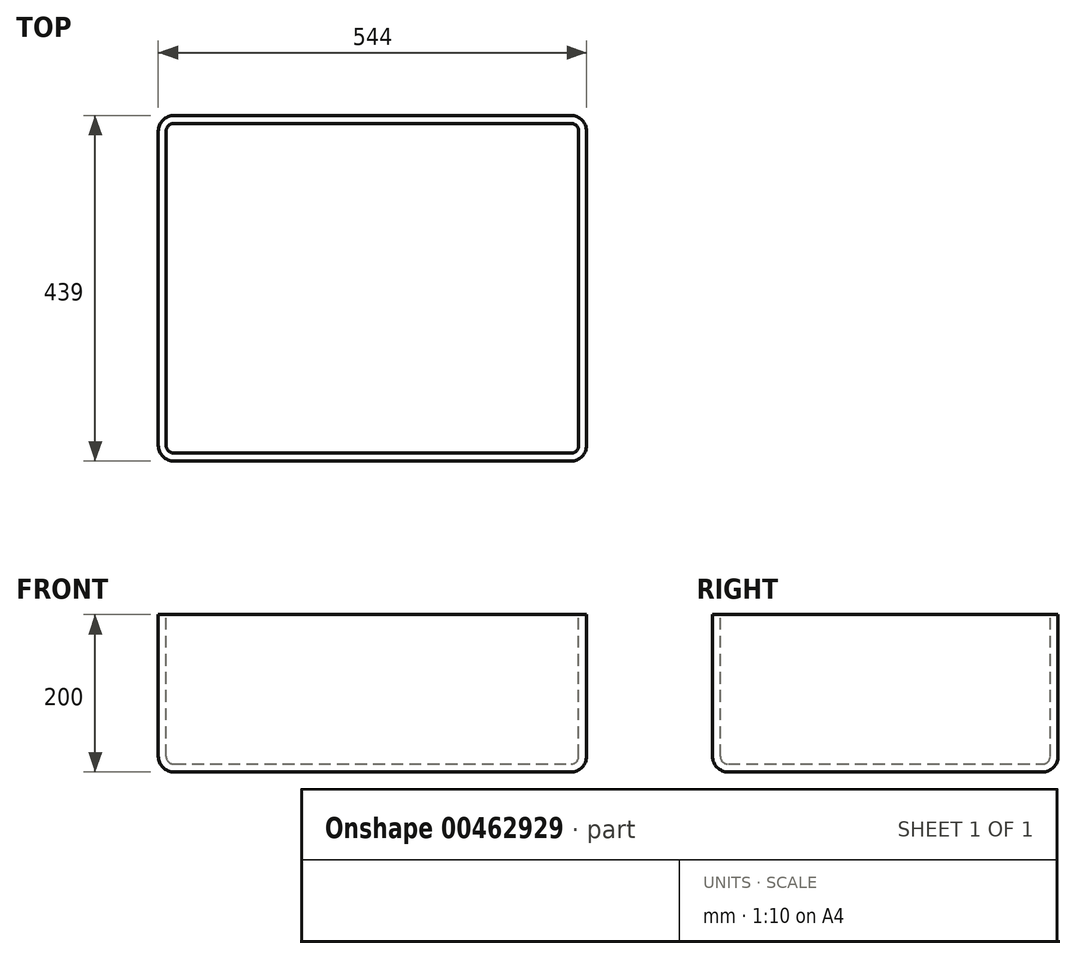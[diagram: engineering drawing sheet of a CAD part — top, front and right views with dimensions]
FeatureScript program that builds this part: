
annotation { "Feature Type Name" : "Feature", "Feature Type Description" : "" }
export const myFeature = defineFeature(function(context is Context, id is Id, definition is map)
    precondition{}
    {
        {
            var Q0;
            Q0=qCreatedBy(makeId("Top.planeOp"),FACE);
            var sketch = newSketch(context, id + "F0", { "sketchPlane" : qUnion([Q0])});
            skLineSegment(sketch, "E0.bottom", {"start": v(-272, -219.5) * mm, "end": v(272, -219.5) * mm});
            skLineSegment(sketch, "E0.top", {"start": v(-272, 219.5) * mm, "end": v(272, 219.5) * mm});
            skLineSegment(sketch, "E0.left", {"start": v(-272, -219.5) * mm, "end": v(-272, 219.5) * mm});
            skLineSegment(sketch, "E0.right", {"start": v(272, -219.5) * mm, "end": v(272, 219.5) * mm});
            skPoint(sketch, "E0.middle", {"position": v(0, 0) * mm});
            skSolve(sketch);
        }
        {
            var Q0;
            Q0 = qSketchRegion(id + "F0", true);
            extrude(context, id + "F1", {"entities" : qUnion([Q0]), "depth" : 200 * mm});
        }
        {
            var Q0;
            Q0=makeQuery(id+"F1.opExtrude","SWEPT_EDGE",EDGE,{"disambiguationData":[OSD([sQuery(id+"F0.wireOp",EDGE,"E0.bottom"),sQuery(id+"F0.wireOp",EDGE,"E0.left")])]});
            var Q1;
            Q1=makeQuery(id+"F1.opExtrude","SWEPT_EDGE",EDGE,{"disambiguationData":[OSD([sQuery(id+"F0.wireOp",EDGE,"E0.bottom"),sQuery(id+"F0.wireOp",EDGE,"E0.right")])]});
            var Q2;
            Q2=makeQuery(id+"F1.opExtrude","SWEPT_EDGE",EDGE,{"disambiguationData":[OSD([sQuery(id+"F0.wireOp",EDGE,"E0.top"),sQuery(id+"F0.wireOp",EDGE,"E0.right")])]});
            var Q3;
            Q3=makeQuery(id+"F1.opExtrude","SWEPT_EDGE",EDGE,{"disambiguationData":[OSD([sQuery(id+"F0.wireOp",EDGE,"E0.top"),sQuery(id+"F0.wireOp",EDGE,"E0.left")])]});
            fillet(context, id + "F2", {"entities" : qUnion([Q0, Q1, Q2, Q3]), "radius" : 20 * mm, "tangentPropagation" : true, "allowEdgeOverflow" : false});
        }
        {
            var Q0;
            Q0=makeQuery(id+"F1.opExtrude","CAP_EDGE",EDGE,{"disambiguationData":[OSD([sQuery(id+"F0.wireOp",EDGE,"E0.top")])],"isStart":true});
            fillet(context, id + "F3", {"entities" : qUnion([Q0]), "radius" : 20 * mm, "tangentPropagation" : true, "allowEdgeOverflow" : false});
        }
        {
            var Q0;
            Q0=makeQuery(id+"F1.opExtrude","CAP_FACE",FACE,{"disambiguationData":[OSD([sQuery(id+"F0.wireOp",EDGE,"E0.bottom"),sQuery(id+"F0.wireOp",EDGE,"E0.top"),sQuery(id+"F0.wireOp",EDGE,"E0.left"),sQuery(id+"F0.wireOp",EDGE,"E0.right")])],"isStart":false});
            shell(context, id + "F4", {"entities" : qUnion([Q0]), "thickness" : 10 * mm});
        }
    });
